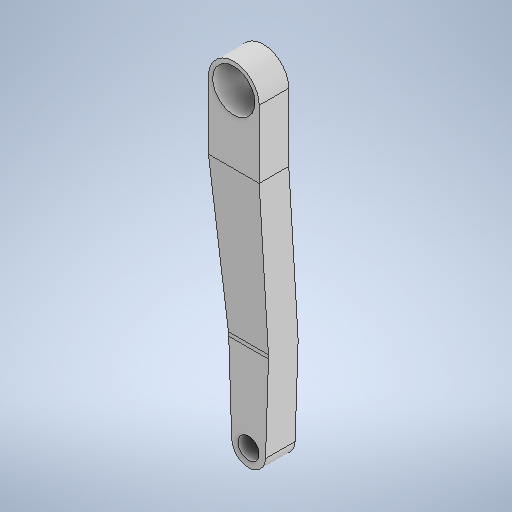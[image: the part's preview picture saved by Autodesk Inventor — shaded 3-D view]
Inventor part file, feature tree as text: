
AUTODESK INVENTOR PART (.ipt)
format: ipt  version: 2025.1 (Build 291241000, 241)  size: 315,392 bytes
history: native  units: mm
features: sketch x5, extrude x3, hole x2, fillet x1, projected_geometry x1
ambient origin geometry x8: Origin, YZ Plane, XZ Plane, XY Plane, X Axis, Y Axis, Z Axis, Center Point
bodies: Body1 (feature_tree)
feature tree (12):
  extrude  "Extrusion7"  Depth=10.0mm
  extrude  "Extrusion8"  Depth=3.5mm
  extrude  "Extrusion9"  Depth=22.0mm
  hole  "Hole1"  [1 undecoded]
  hole  "Hole2"  [1 undecoded]
  fillet  "Fillet1"  Radius=8.0mm
  sketch  "Sketch19"  dims[d79=10.0mm d80=10.0mm]
  sketch  "Sketch20"  dims[d82=7.0mm d83=3.5mm]
  sketch  "Sketch21"  dims[d84=24.6mm d85=22.0mm]
  projected_geometry  "Projected Loop13"
  sketch  "Sketch22"  dims[d86=37.940206mm d87=12.0mm d88=0.0mm]
  sketch  "Sketch23"  dims[d89=12.0mm d90=12.0mm d91=0.0mm d93=8.0mm d94=12.0mm d95=0.0mm d96=10.0mm d97=6.0mm d98=4.0mm d99=2.0mm d100=90.0deg d101=8.0mm d102=20.594885mm d103=5.0mm d104=6.0mm d105=4.0mm d106=2.0mm d107=90.0deg d108=8.0mm d109=20.594885mm d110=10.0mm d92=0.0mm]
note: 2 required parameter values undecoded (feature->parameter linkage not recoverable at this tier; creation-order binding heuristic only, values carry confidence <= 0.55)
